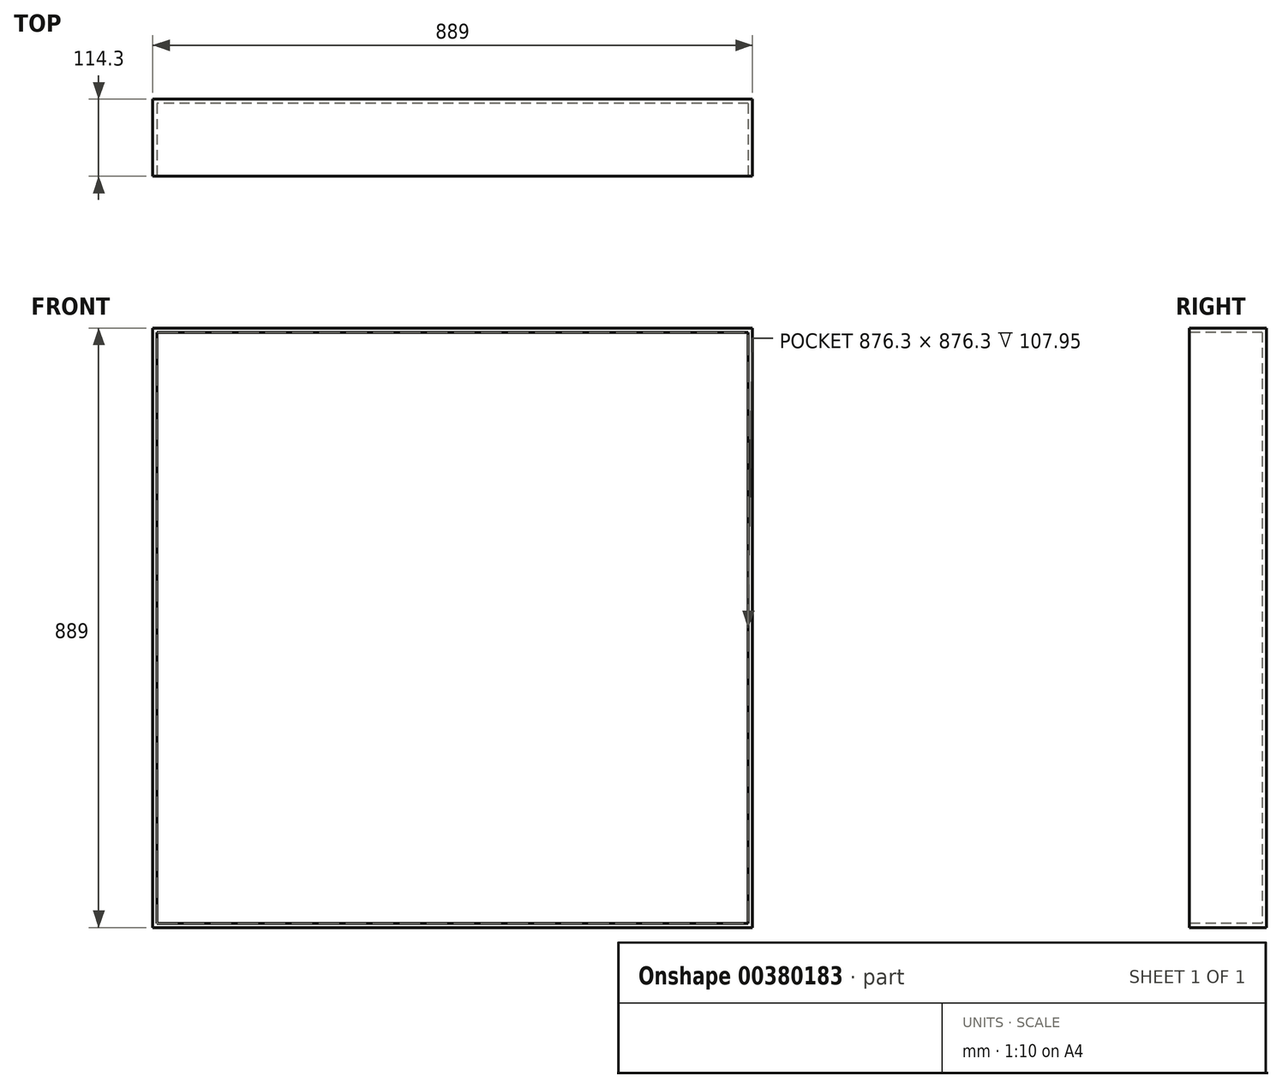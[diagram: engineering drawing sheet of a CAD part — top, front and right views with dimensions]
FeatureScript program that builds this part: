
annotation { "Feature Type Name" : "Feature", "Feature Type Description" : "" }
export const myFeature = defineFeature(function(context is Context, id is Id, definition is map)
    precondition{}
    {
        {
            var Q0;
            Q0=qCreatedBy(makeId("Front.planeOp"),FACE);
            var sketch = newSketch(context, id + "F0", { "sketchPlane" : qUnion([Q0])});
            skLineSegment(sketch, "E0.bottom", {"start": v(444.5, 444.5) * mm, "end": v(-444.5, 444.5) * mm});
            skLineSegment(sketch, "E0.top", {"start": v(444.5, -444.5) * mm, "end": v(-444.5, -444.5) * mm});
            skLineSegment(sketch, "E0.left", {"start": v(444.5, 444.5) * mm, "end": v(444.5, -444.5) * mm});
            skLineSegment(sketch, "E0.right", {"start": v(-444.5, 444.5) * mm, "end": v(-444.5, -444.5) * mm});
            skPoint(sketch, "E0.middle", {"position": v(0, 0) * mm});
            skSolve(sketch);
        }
        {
            var Q0;
            Q0 = qSketchRegion(id + "F0", true);
            extrude(context, id + "F1", {"entities" : qUnion([Q0]), "oppositeDirection" : true, "depth" : 114.3 * mm});
        }
        {
            var Q0;
            Q0=makeQuery(id+"F1.opExtrude","CAP_FACE",FACE,{"disambiguationData":[OSD([sQuery(id+"F0.wireOp",EDGE,"E0.bottom"),sQuery(id+"F0.wireOp",EDGE,"E0.top"),sQuery(id+"F0.wireOp",EDGE,"E0.left"),sQuery(id+"F0.wireOp",EDGE,"E0.right")])],"isStart":true});
            shell(context, id + "F2", {"entities" : qUnion([Q0]), "thickness" : 6.35 * mm});
        }
    });
